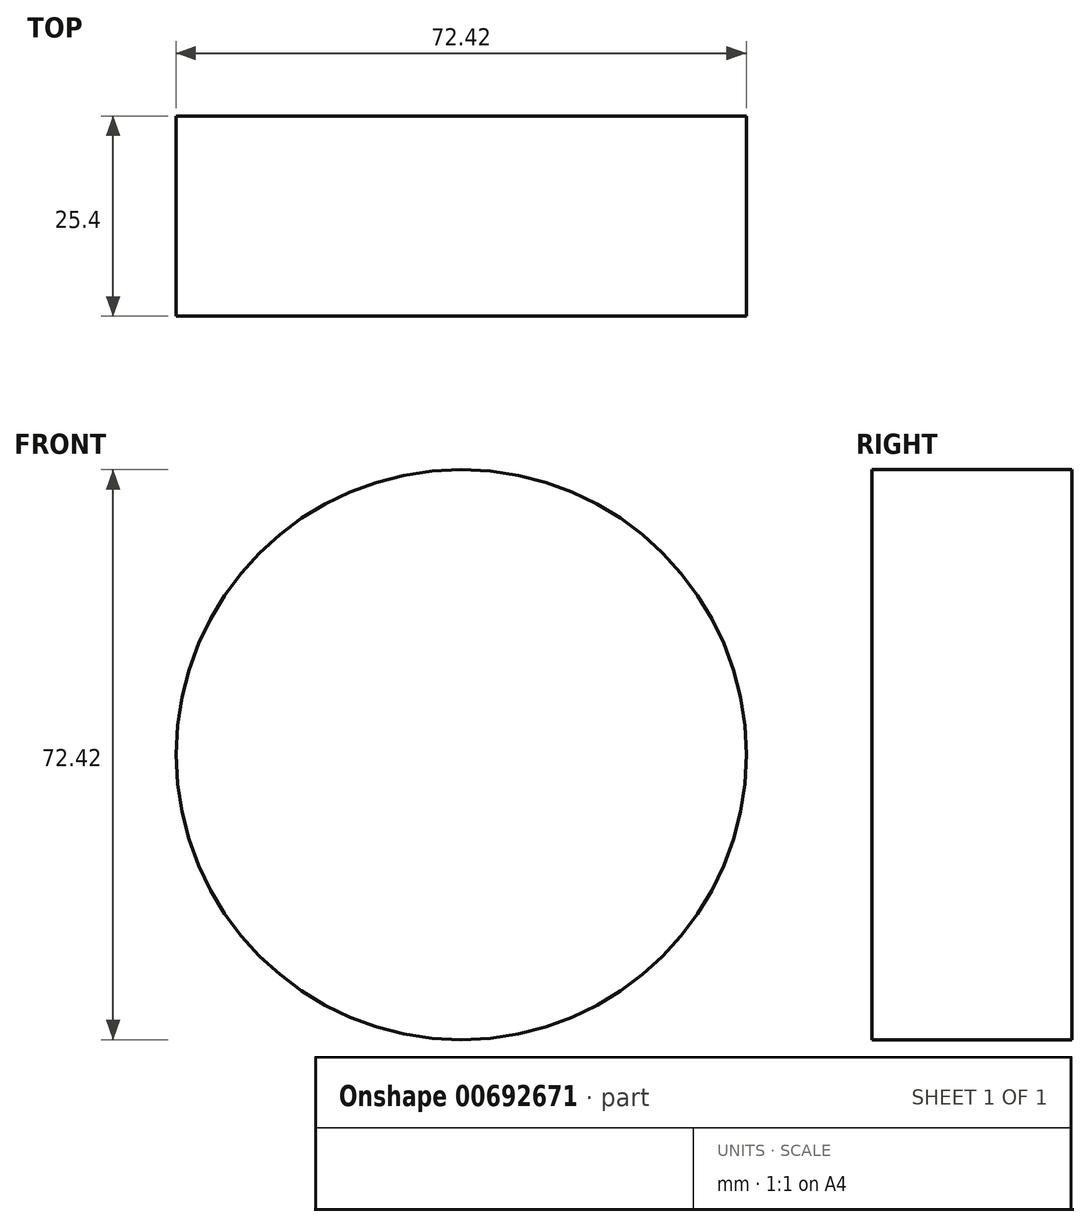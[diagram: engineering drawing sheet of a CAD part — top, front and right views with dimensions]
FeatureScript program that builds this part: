
annotation { "Feature Type Name" : "Feature", "Feature Type Description" : "" }
export const myFeature = defineFeature(function(context is Context, id is Id, definition is map)
    precondition{}
    {
        {
            var Q0;
            Q0=qCreatedBy(makeId("Front.planeOp"),FACE);
            var sketch = newSketch(context, id + "F0", { "sketchPlane" : qUnion([Q0])});
            skCircle(sketch, "E0", {"center": v(0, 0) * mm, "radius": 36.21 * mm});
            skSolve(sketch);
        }
        {
            var Q0;
            Q0 = qSketchRegion(id + "F0", true);
            extrude(context, id + "F1", {"entities" : qUnion([Q0]), "depth" : 25.4 * mm, "offsetDistance" : 25.4 * mm});
        }
    });
